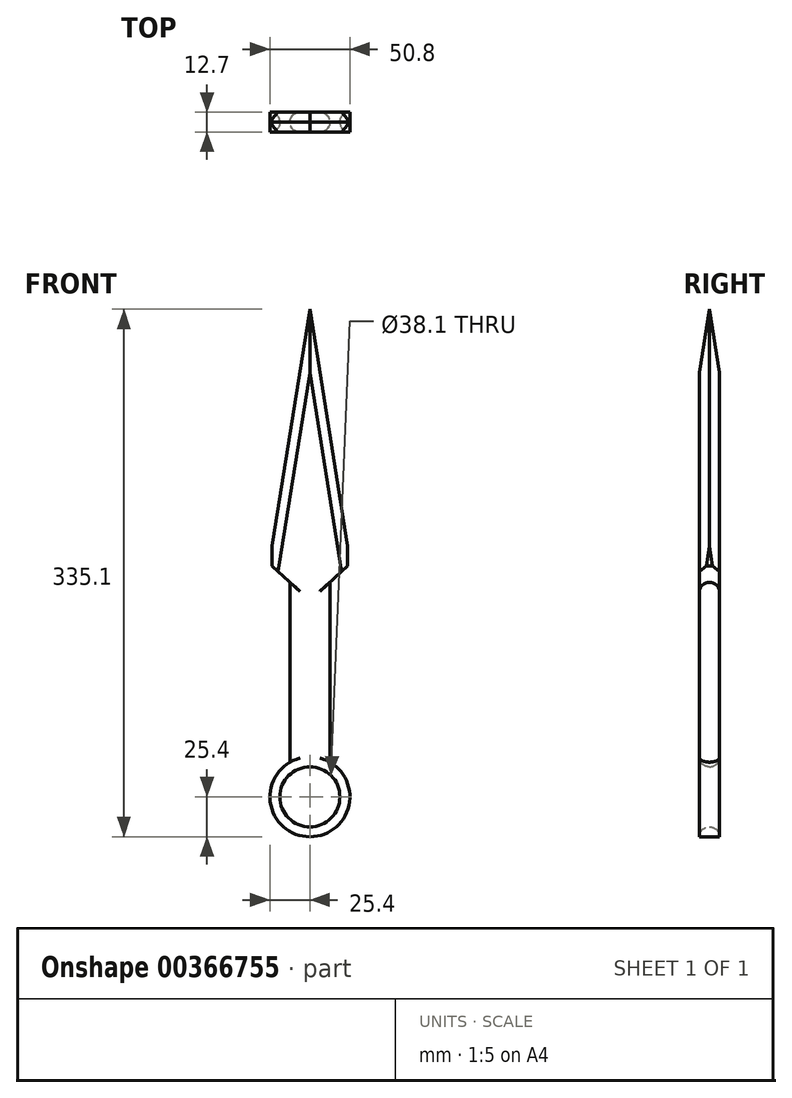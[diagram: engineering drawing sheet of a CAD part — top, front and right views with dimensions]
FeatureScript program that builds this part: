
annotation { "Feature Type Name" : "Feature", "Feature Type Description" : "" }
export const myFeature = defineFeature(function(context is Context, id is Id, definition is map)
    precondition{}
    {
        {
            var Q0;
            Q0=qCreatedBy(makeId("Front.planeOp"),FACE);
            var sketch = newSketch(context, id + "F0", { "sketchPlane" : qUnion([Q0])});
            skCircle(sketch, "E0", {"center": v(0, 0) * mm, "radius": 19.05 * mm});
            skCircle(sketch, "E1", {"center": v(0, 0) * mm, "radius": 25.4 * mm});
            skLineSegment(sketch, "E2", {"start": v(-12.7, 22) * mm, "end": v(-12.7, 136.3) * mm});
            skLineSegment(sketch, "E3", {"start": v(-12.7, 136.3) * mm, "end": v(-24.02, 146.5) * mm});
            skLineSegment(sketch, "E4.MirrorCS", {"start": v(12.7, 22) * mm, "end": v(12.7, 136.3) * mm});
            skLineSegment(sketch, "E5.MirrorCS", {"start": v(12.7, 136.3) * mm, "end": v(24.02, 146.5) * mm});
            skLineSegment(sketch, "E6", {"start": v(-24.02, 146.5) * mm, "end": v(-24.02, 159.2) * mm});
            skLineSegment(sketch, "E7.MirrorCS", {"start": v(24.02, 146.5) * mm, "end": v(24.02, 159.2) * mm});
            skLineSegment(sketch, "E8", {"start": v(-24.02, 159.2) * mm, "end": v(24.02, 159.2) * mm});
            skLineSegment(sketch, "E9", {"start": v(24.02, 159.2) * mm, "end": v(0, 309.7) * mm});
            skLineSegment(sketch, "E10", {"start": v(0, 309.7) * mm, "end": v(-24.02, 159.2) * mm});
            skSolve(sketch);
        }
        {
            var Q0;
            Q0=qSketchRegion(id+"F0",true);
            extrude(context, id + "F1", {"entities" : qUnion([Q0]), "depth" : 12.7 * mm});
        }
        {
            var Q0;
            Q0=makeQuery(id+"F1.opExtrude","CAP_EDGE",EDGE,{"disambiguationData":[OSD([sQuery(id+"F0.wireOp",EDGE,"E10")])],"isStart":false});
            var Q1;
            Q1=makeQuery(id+"F1.opExtrude","CAP_EDGE",EDGE,{"disambiguationData":[OSD([sQuery(id+"F0.wireOp",EDGE,"E9")])],"isStart":false});
            var Q2;
            Q2=makeQuery(id+"F1.opExtrude","CAP_EDGE",EDGE,{"disambiguationData":[OSD([sQuery(id+"F0.wireOp",EDGE,"E9")])],"isStart":true});
            var Q3;
            Q3=makeQuery(id+"F1.opExtrude","CAP_EDGE",EDGE,{"disambiguationData":[OSD([sQuery(id+"F0.wireOp",EDGE,"E10")])],"isStart":true});
            chamfer(context, id + "F2", {"entities" : qUnion([Q0, Q1, Q2, Q3]), "chamferType" : ChamferType.OFFSET_ANGLE, "width" : 6.35 * mm, "oppositeDirection" : false, "angle" : 45 * degree, "tangentPropagation" : true});
        }
        {
            var Q0;
            Q0=makeQuery(id+"F1.opExtrude","CAP_EDGE",EDGE,{"disambiguationData":[OSD([sQuery(id+"F0.wireOp",EDGE,"E4.MirrorCS")])],"isStart":true});
            var Q1;
            Q1=makeQuery(id+"F1.opExtrude","CAP_EDGE",EDGE,{"disambiguationData":[OSD([sQuery(id+"F0.wireOp",EDGE,"E4.MirrorCS")])],"isStart":false});
            var Q2;
            Q2=makeQuery(id+"F1.opExtrude","CAP_EDGE",EDGE,{"disambiguationData":[OSD([sQuery(id+"F0.wireOp",EDGE,"E2")])],"isStart":false});
            var Q3;
            Q3=makeQuery(id+"F1.opExtrude","CAP_EDGE",EDGE,{"disambiguationData":[OSD([sQuery(id+"F0.wireOp",EDGE,"E2")])],"isStart":true});
            fillet(context, id + "F3", {"entities" : qUnion([Q0, Q1, Q2, Q3]), "radius" : 6.35 * mm, "tangentPropagation" : true, "allowEdgeOverflow" : false});
        }
        {
            var Q0;
            Q0=makeQuery(id+"F1.opExtrude","CAP_EDGE",EDGE,{"disambiguationData":[OSD([sQuery(id+"F0.wireOp",EDGE,"E0")])],"isStart":true});
            var Q1;
            Q1=makeQuery(id+"F1.opExtrude","CAP_EDGE",EDGE,{"disambiguationData":[OSD([sQuery(id+"F0.wireOp",EDGE,"E0")])],"isStart":false});
            fillet(context, id + "F4", {"entities" : qUnion([Q0, Q1]), "radius" : 6.32 * mm, "tangentPropagation" : true, "allowEdgeOverflow" : false});
        }
    });
